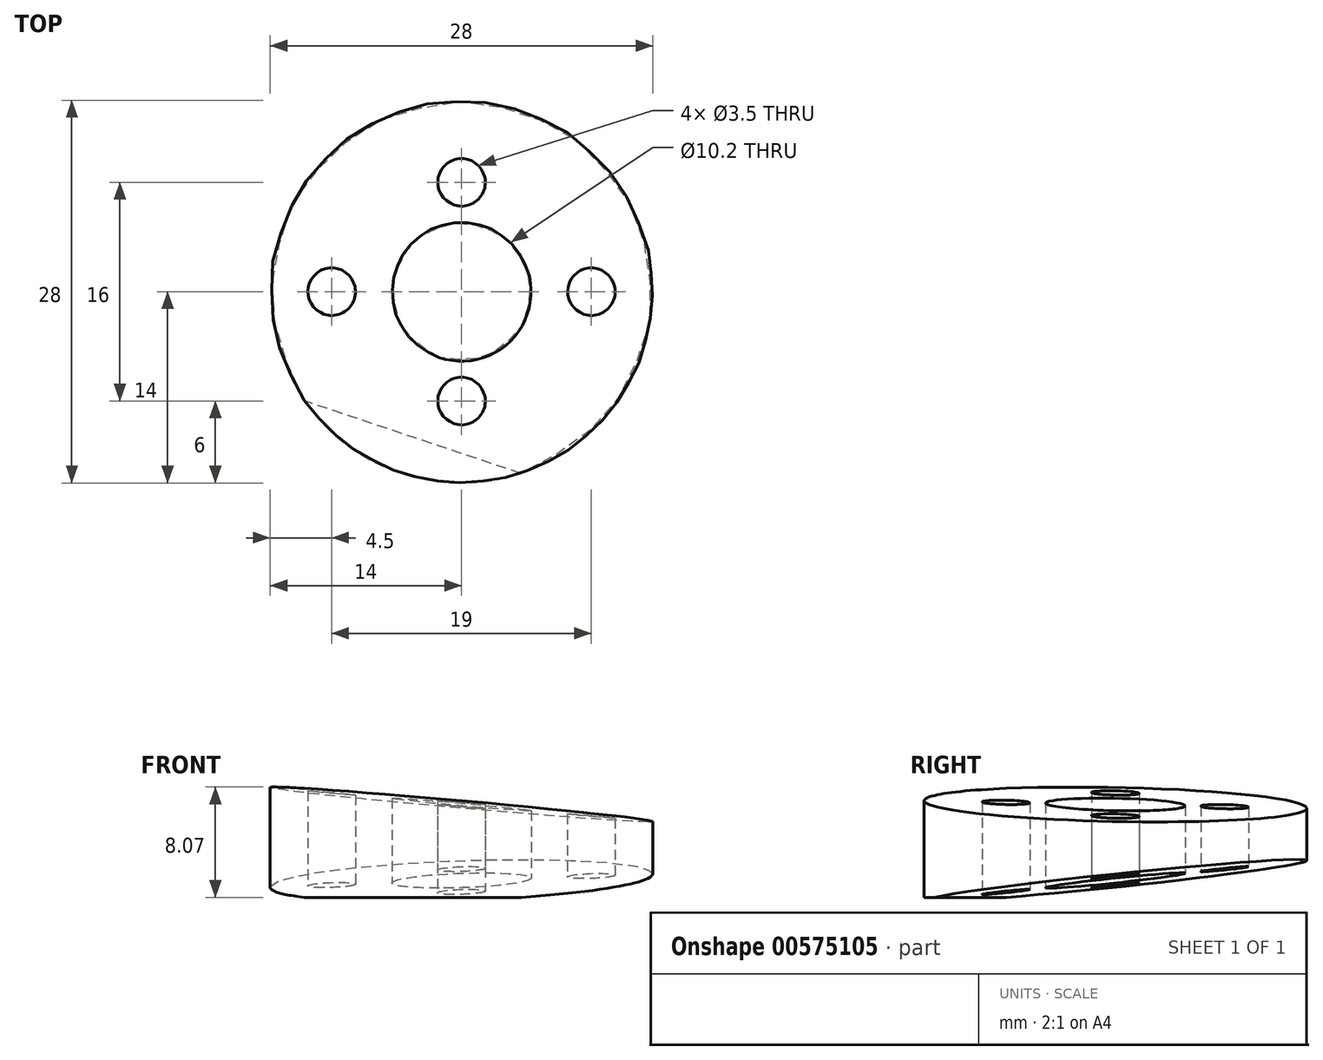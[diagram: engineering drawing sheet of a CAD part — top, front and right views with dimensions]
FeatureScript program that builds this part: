
annotation { "Feature Type Name" : "Feature", "Feature Type Description" : "" }
export const myFeature = defineFeature(function(context is Context, id is Id, definition is map)
    precondition{}
    {
        {
            var Q0;
            Q0=qCreatedBy(makeId("Top.planeOp"),FACE);
            var sketch = newSketch(context, id + "F0", { "sketchPlane" : qUnion([Q0])});
            skCircle(sketch, "E0", {"center": v(0, 0) * mm, "radius": 14 * mm});
            skCircle(sketch, "E1", {"center": v(0, 0) * mm, "radius": 8 * mm, "construction": true});
            skCircle(sketch, "E2", {"center": v(0, 0) * mm, "radius": 9.5 * mm, "construction": true});
            skCircle(sketch, "E3", {"center": v(0, 8) * mm, "radius": 1.75 * mm});
            skCircle(sketch, "E4", {"center": v(0, -8) * mm, "radius": 1.75 * mm});
            skCircle(sketch, "E5", {"center": v(-9.5, 0) * mm, "radius": 1.75 * mm});
            skCircle(sketch, "E6", {"center": v(9.5, 0) * mm, "radius": 1.75 * mm});
            skCircle(sketch, "E7", {"center": v(0, 0) * mm, "radius": 5.1 * mm});
            skSolve(sketch);
        }
        {
            var Q0;
            Q0=qSketchRegion(id+"F0",true);
            extrude(context, id + "F1", {"entities" : qUnion([Q0]), "depth" : 10 * mm, "offsetDistance" : 25 * mm});
        }
        {
            var Q0;
            Q0=qCreatedBy(makeId("Top.planeOp"),FACE);
            var sketch = newSketch(context, id + "F2", { "sketchPlane" : qUnion([Q0])});
            skLineSegment(sketch, "E8", {"start": v(30.34, 30.34) * mm, "end": v(-30.72, -30.72) * mm, "construction": true});
            skLineSegment(sketch, "E9", {"start": v(0, 0) * mm, "end": v(26.2, -26.2) * mm, "construction": true});
            skSolve(sketch);
        }
        {
            var Q0;
            Q0=sQuery(id+"F2.wireOp",EDGE,"E8");
            cPlane(context, id + "F3", {"entities" : qUnion([Q0]), "cplaneType" : CPlaneType.LINE_ANGLE, "offset" : 25 * mm, "angle" : 87.2 * degree, "width" : 150 * mm, "height" : 150 * mm});
        }
        {
            var Q0;
            Q0=qCreatedBy(id+"F3.planeOp",FACE);
            cPlane(context, id + "F4", {"entities" : qUnion([Q0]), "cplaneType" : CPlaneType.OFFSET, "offset" : 25 * mm, "width" : 150 * mm, "height" : 150 * mm});
        }
        {
            var Q0;
            Q0=qCreatedBy(id+"F4.planeOp",FACE);
            var sketch = newSketch(context, id + "F5", { "sketchPlane" : qUnion([Q0])});
            skLineSegment(sketch, "E10", {"start": v(-41.52, -0.8) * mm, "end": v(31.92, 2.8) * mm});
            skLineSegment(sketch, "E11", {"start": v(31.92, 2.8) * mm, "end": v(-42.16, 12.14) * mm});
            skLineSegment(sketch, "E12", {"start": v(-42.16, 12.14) * mm, "end": v(-41.52, -0.8) * mm});
            skLineSegment(sketch, "E13", {"start": v(14.92, 1.96) * mm, "end": v(14.78, 4.96) * mm});
            skSolve(sketch);
        }
        {
            var Q0;
            Q0=qSketchRegion(id+"F5",true);
            extrude(context, id + "F6", {"entities" : qUnion([Q0]), "operationType" : NewBodyOperationType.INTERSECT, "oppositeDirection" : true, "depth" : 40 * mm, "offsetDistance" : 25 * mm});
        }
    });
